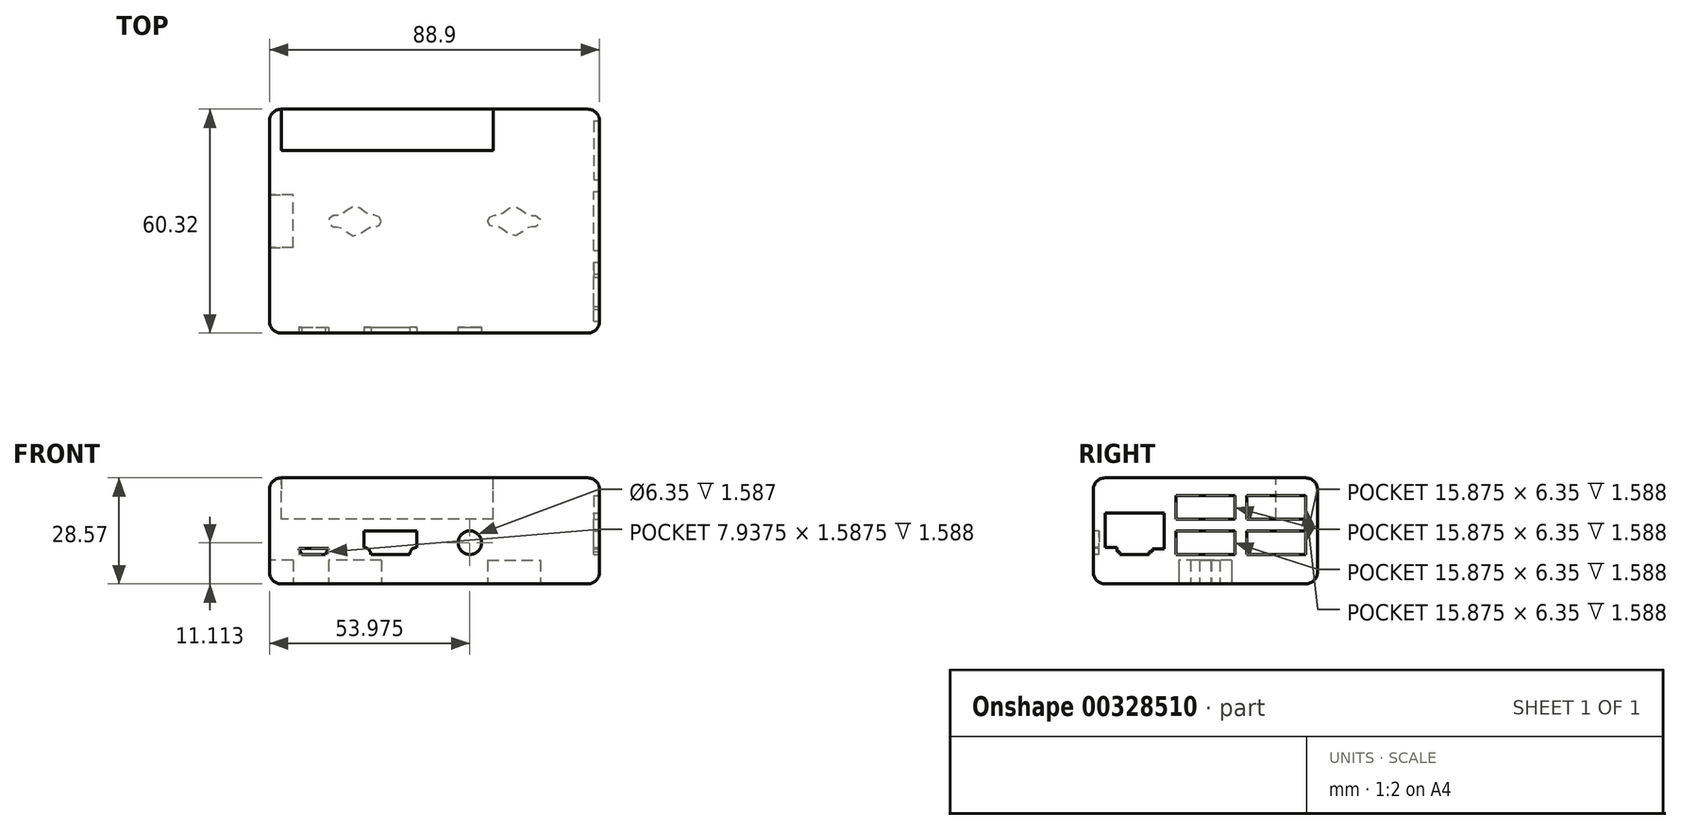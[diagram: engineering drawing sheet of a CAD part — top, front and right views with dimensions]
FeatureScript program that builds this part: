
annotation { "Feature Type Name" : "Feature", "Feature Type Description" : "" }
export const myFeature = defineFeature(function(context is Context, id is Id, definition is map)
    precondition{}
    {
        {
            var Q0;
            Q0=qCreatedBy(makeId("Top.planeOp"),FACE);
            var sketch = newSketch(context, id + "F0", { "sketchPlane" : qUnion([Q0])});
            skLineSegment(sketch, "E0.bottom", {"start": v(44.45, 30.16) * mm, "end": v(-44.45, 30.16) * mm});
            skLineSegment(sketch, "E0.top", {"start": v(44.45, -30.16) * mm, "end": v(-44.45, -30.16) * mm});
            skLineSegment(sketch, "E0.left", {"start": v(44.45, 30.16) * mm, "end": v(44.45, -30.16) * mm});
            skLineSegment(sketch, "E0.right", {"start": v(-44.45, 30.16) * mm, "end": v(-44.45, -30.16) * mm});
            skPoint(sketch, "E0.middle", {"position": v(0, 0) * mm});
            skLineSegment(sketch, "E1", {"start": v(0, 0) * mm, "end": v(14.29, 0) * mm});
            skLineSegment(sketch, "E2", {"start": v(0, 0) * mm, "end": v(-14.29, 0) * mm});
            skLineSegment(sketch, "E3", {"start": v(-14.29, 0) * mm, "end": v(-28.58, 0) * mm, "construction": true});
            skLineSegment(sketch, "E4", {"start": v(14.29, 0) * mm, "end": v(28.58, 0) * mm, "construction": true});
            skPoint(sketch, "E5", {"position": v(21.43, 0) * mm});
            skPoint(sketch, "E6", {"position": v(-21.43, 0) * mm});
            skLineSegment(sketch, "E7", {"start": v(14.29, 0) * mm, "end": v(15.88, 0) * mm, "construction": true});
            skLineSegment(sketch, "E8", {"start": v(28.58, 0) * mm, "end": v(26.99, 0) * mm, "construction": true});
            skLineSegment(sketch, "E9", {"start": v(-28.58, 0) * mm, "end": v(-26.99, 0) * mm, "construction": true});
            skLineSegment(sketch, "E10", {"start": v(-14.29, 0) * mm, "end": v(-15.88, 0) * mm, "construction": true});
            skLineSegment(sketch, "E11", {"start": v(-15.88, 0) * mm, "end": v(-15.88, 1.59) * mm, "construction": true});
            skLineSegment(sketch, "E12", {"start": v(-26.99, 0) * mm, "end": v(-26.99, 1.59) * mm, "construction": true});
            skLineSegment(sketch, "E13", {"start": v(-26.99, 0) * mm, "end": v(-26.99, -1.59) * mm, "construction": true});
            skLineSegment(sketch, "E14", {"start": v(-15.88, 0) * mm, "end": v(-15.88, -1.59) * mm, "construction": true});
            skLineSegment(sketch, "E15", {"start": v(15.88, 0) * mm, "end": v(15.88, -1.59) * mm, "construction": true});
            skLineSegment(sketch, "E16", {"start": v(26.99, 0) * mm, "end": v(26.99, 1.59) * mm, "construction": true});
            skLineSegment(sketch, "E17", {"start": v(15.88, 0) * mm, "end": v(15.88, 1.59) * mm, "construction": true});
            skLineSegment(sketch, "E18", {"start": v(26.99, 0) * mm, "end": v(26.99, -1.59) * mm, "construction": true});
            skLineSegment(sketch, "E19", {"start": v(21.43, 0) * mm, "end": v(21.43, 3.97) * mm, "construction": true});
            skLineSegment(sketch, "E20", {"start": v(21.43, 0) * mm, "end": v(21.43, -3.97) * mm, "construction": true});
            skLineSegment(sketch, "E21", {"start": v(15.88, 1.59) * mm, "end": v(17.46, 1.59) * mm, "construction": true});
            skLineSegment(sketch, "E22", {"start": v(15.88, -1.59) * mm, "end": v(17.46, -1.59) * mm, "construction": true});
            skLineSegment(sketch, "E23", {"start": v(26.99, 1.59) * mm, "end": v(25.4, 1.59) * mm, "construction": true});
            skLineSegment(sketch, "E24", {"start": v(26.99, -1.59) * mm, "end": v(25.4, -1.59) * mm, "construction": true});
            skFitSpline(sketch, "E25", {"points": [v(14.29, 0) * mm, v(15.88, 1.59) * mm, v(17.46, 1.59) * mm, v(21.43, 3.97) * mm, v(25.4, 1.59) * mm, v(26.99, 1.59) * mm, v(28.58, 0) * mm, v(26.99, -1.59) * mm, v(25.4, -1.59) * mm, v(21.43, -3.97) * mm, v(17.46, -1.59) * mm, v(15.88, -1.59) * mm, v(14.29, 0) * mm]});
            skLineSegment(sketch, "E26", {"start": v(0, 0) * mm, "end": v(0, 11.35) * mm, "construction": true});
            skLineSegment(sketch, "E27.MirrorCS", {"start": v(-15.88, 1.59) * mm, "end": v(-17.46, 1.59) * mm, "construction": true});
            skLineSegment(sketch, "E28.MirrorCS", {"start": v(-15.88, -1.59) * mm, "end": v(-17.46, -1.59) * mm, "construction": true});
            skLineSegment(sketch, "E29.MirrorCS", {"start": v(-26.99, -1.59) * mm, "end": v(-25.4, -1.59) * mm, "construction": true});
            skLineSegment(sketch, "E30.MirrorCS", {"start": v(-26.99, 1.59) * mm, "end": v(-25.4, 1.59) * mm, "construction": true});
            skLineSegment(sketch, "E31.MirrorCS", {"start": v(-21.43, 0) * mm, "end": v(-21.43, 3.97) * mm, "construction": true});
            skLineSegment(sketch, "E32.MirrorCS", {"start": v(-21.43, 0) * mm, "end": v(-21.43, -3.97) * mm, "construction": true});
            skFitSpline(sketch, "E33.MirrorC", {"points": [v(-14.29, 0) * mm, v(-15.88, 1.59) * mm, v(-17.46, 1.59) * mm, v(-21.43, 3.97) * mm, v(-25.4, 1.59) * mm, v(-26.99, 1.59) * mm, v(-28.58, 0) * mm, v(-26.99, -1.59) * mm, v(-25.4, -1.59) * mm, v(-21.43, -3.97) * mm, v(-17.46, -1.59) * mm, v(-15.88, -1.59) * mm, v(-14.29, 0) * mm]});
            skLineSegment(sketch, "E34", {"start": v(-44.45, 0) * mm, "end": v(-38.1, 0) * mm});
            skLineSegment(sketch, "E35", {"start": v(-38.1, 0) * mm, "end": v(-38.1, 7.14) * mm});
            skLineSegment(sketch, "E36", {"start": v(-38.1, 0) * mm, "end": v(-38.1, -7.14) * mm});
            skLineSegment(sketch, "E37", {"start": v(-38.1, -7.14) * mm, "end": v(-44.45, -7.14) * mm});
            skLineSegment(sketch, "E38", {"start": v(-38.1, 7.14) * mm, "end": v(-44.45, 7.14) * mm});
            skSolve(sketch);
        }
        {
            var Q0;
            Q0 = qSketchRegion(id + "F0", true);
            var Q1;
            Q1=makeQuery(id+"F0.imprint","IMPRINT",FACE,{"disambiguationData":[TD([[makeQuery(id+"F0.imprint","IMPRINT",EDGE,{"derivedFrom":sQuery(id+"F0.wireOp",EDGE,"E33.MirrorC")}),1.0]])]});
            var Q2;
            Q2=makeQuery(id+"F0.imprint","IMPRINT",FACE,{"disambiguationData":[TD([[makeQuery(id+"F0.imprint","IMPRINT",EDGE,{"derivedFrom":sQuery(id+"F0.wireOp",EDGE,"E25")}),-1.0]])]});
            extrude(context, id + "F1", {"entities" : qUnion([Q0, Q1, Q2]), "depth" : 28.57 * mm});
        }
        {
            var Q0;
            {var subQ0=sQuery(id+"F0.wireOp",EDGE,"E34");Q0=makeQuery(id+"F0.imprint","IMPRINT",FACE,{"disambiguationData":[TD([[makeQuery(id+"F0.imprint","IMPRINT",EDGE,{"derivedFrom":subQ0}),1.0]])]});}
            var Q1;
            {var subQ0=sQuery(id+"F0.wireOp",EDGE,"E34");Q1=makeQuery(id+"F0.imprint","IMPRINT",FACE,{"disambiguationData":[TD([[makeQuery(id+"F0.imprint","IMPRINT",EDGE,{"derivedFrom":subQ0}),-1.0]])]});}
            var Q2;
            Q2=makeQuery(id+"F0.imprint","IMPRINT",FACE,{"disambiguationData":[TD([[makeQuery(id+"F0.imprint","IMPRINT",EDGE,{"derivedFrom":sQuery(id+"F0.wireOp",EDGE,"E33.MirrorC")}),1.0]])]});
            var Q3;
            Q3=makeQuery(id+"F0.imprint","IMPRINT",FACE,{"disambiguationData":[TD([[makeQuery(id+"F0.imprint","IMPRINT",EDGE,{"derivedFrom":sQuery(id+"F0.wireOp",EDGE,"E25")}),-1.0]])]});
            extrude(context, id + "F2", {"entities" : qUnion([Q0, Q1, Q2, Q3]), "operationType" : NewBodyOperationType.REMOVE, "depth" : 6.35 * mm});
        }
        {
            var Q0;
            Q0=makeQuery(id+"F1.opExtrude","SWEPT_FACE",FACE,{"disambiguationData":[OSD([sQuery(id+"F0.wireOp",EDGE,"E0.top")])]});
            var sketch = newSketch(context, id + "F3", { "sketchPlane" : qUnion([Q0])});
            skLineSegment(sketch, "E39.0.0", {"start": v(-44.45, 0) * mm, "end": v(44.45, 0) * mm});
            skLineSegment(sketch, "E39.0.1", {"start": v(44.45, 0) * mm, "end": v(44.45, 28.58) * mm});
            skLineSegment(sketch, "E39.0.2", {"start": v(44.45, 28.58) * mm, "end": v(-44.45, 28.58) * mm});
            skLineSegment(sketch, "E39.0.3", {"start": v(-44.45, 28.58) * mm, "end": v(-44.45, 0) * mm});
            skLineSegment(sketch, "E40", {"start": v(-44.45, 0) * mm, "end": v(-44.45, 14.29) * mm, "construction": true});
            skLineSegment(sketch, "E41", {"start": v(-44.45, 14.29) * mm, "end": v(44.45, 14.29) * mm, "construction": true});
            skLineSegment(sketch, "E42", {"start": v(-44.45, 14.29) * mm, "end": v(-44.45, 7.94) * mm, "construction": true});
            skLineSegment(sketch, "E43", {"start": v(-44.45, 7.94) * mm, "end": v(44.45, 7.94) * mm, "construction": true});
            skLineSegment(sketch, "E44", {"start": v(-44.45, 14.29) * mm, "end": v(-19.05, 14.29) * mm, "construction": true});
            skLineSegment(sketch, "E45", {"start": v(-19.05, 14.29) * mm, "end": v(-4.76, 14.29) * mm, "construction": true});
            skLineSegment(sketch, "E46", {"start": v(-4.76, 14.29) * mm, "end": v(-4.76, 9.84) * mm, "construction": true});
            skLineSegment(sketch, "E47", {"start": v(-19.05, 14.29) * mm, "end": v(-19.05, 9.84) * mm});
            skLineSegment(sketch, "E48", {"start": v(-19.05, 14.29) * mm, "end": v(-4.76, 14.29) * mm});
            skLineSegment(sketch, "E49", {"start": v(-4.76, 14.29) * mm, "end": v(-4.76, 9.84) * mm});
            skLineSegment(sketch, "E50", {"start": v(-4.76, 14.29) * mm, "end": v(-6.35, 14.29) * mm, "construction": true});
            skLineSegment(sketch, "E51", {"start": v(-19.05, 14.29) * mm, "end": v(-17.46, 14.29) * mm, "construction": true});
            skLineSegment(sketch, "E52", {"start": v(-17.46, 14.29) * mm, "end": v(-17.46, 7.94) * mm, "construction": true});
            skLineSegment(sketch, "E53", {"start": v(-6.35, 14.29) * mm, "end": v(-6.35, 7.94) * mm, "construction": true});
            skLineSegment(sketch, "E54", {"start": v(-17.46, 7.94) * mm, "end": v(-6.35, 7.94) * mm});
            skPoint(sketch, "E55", {"position": v(-4.76, 7.94) * mm});
            skPoint(sketch, "E56", {"position": v(-19.05, 7.94) * mm});
            skArc(sketch, "E57", {"start": v(-19.05, 9.84) * mm, "mid": v(-17.7, 9.28) * mm, "end": v(-17.15, 7.94) * mm});
            skArc(sketch, "E58", {"start": v(-4.76, 9.84) * mm, "mid": v(-6.1, 9.28) * mm, "end": v(-6.67, 7.94) * mm});
            skLineSegment(sketch, "E59", {"start": v(-44.45, 7.94) * mm, "end": v(-36.51, 7.94) * mm, "construction": true});
            skLineSegment(sketch, "E60", {"start": v(-36.51, 7.94) * mm, "end": v(-28.58, 7.94) * mm, "construction": true});
            skLineSegment(sketch, "E61", {"start": v(-28.58, 7.94) * mm, "end": v(-28.58, 9.52) * mm, "construction": true});
            skLineSegment(sketch, "E62", {"start": v(-28.58, 9.52) * mm, "end": v(-36.51, 9.52) * mm, "construction": true});
            skLineSegment(sketch, "E63", {"start": v(-36.51, 9.52) * mm, "end": v(-36.51, 7.94) * mm, "construction": true});
            skLineSegment(sketch, "E64", {"start": v(-36.51, 9.52) * mm, "end": v(-28.58, 9.52) * mm});
            skLineSegment(sketch, "E65", {"start": v(-36.51, 7.94) * mm, "end": v(-35.72, 7.94) * mm});
            skLineSegment(sketch, "E66", {"start": v(-28.58, 7.94) * mm, "end": v(-29.37, 7.94) * mm});
            skLineSegment(sketch, "E67", {"start": v(-29.37, 7.94) * mm, "end": v(-28.58, 9.52) * mm});
            skLineSegment(sketch, "E68", {"start": v(-35.72, 7.94) * mm, "end": v(-36.51, 9.53) * mm});
            skLineSegment(sketch, "E69", {"start": v(-35.72, 7.94) * mm, "end": v(-29.37, 7.94) * mm});
            skLineSegment(sketch, "E70", {"start": v(-4.76, 14.29) * mm, "end": v(9.53, 14.29) * mm, "construction": true});
            skLineSegment(sketch, "E71", {"start": v(-4.76, 7.94) * mm, "end": v(9.53, 7.94) * mm, "construction": true});
            skLineSegment(sketch, "E72", {"start": v(9.53, 7.94) * mm, "end": v(9.53, 14.29) * mm, "construction": true});
            skPoint(sketch, "E73", {"position": v(9.53, 11.11) * mm});
            skCircle(sketch, "E74", {"center": v(9.53, 11.11) * mm, "radius": 3.18 * mm});
            skSolve(sketch);
        }
        {
            var Q0;
            Q0=makeQuery(id+"F1.opExtrude","SWEPT_FACE",FACE,{"disambiguationData":[OSD([sQuery(id+"F0.wireOp",EDGE,"E0.left")])]});
            var sketch = newSketch(context, id + "F4", { "sketchPlane" : qUnion([Q0])});
            skLineSegment(sketch, "E75", {"start": v(30.16, 0) * mm, "end": v(30.16, 7.94) * mm, "construction": true});
            skLineSegment(sketch, "E76", {"start": v(26.99, 7.94) * mm, "end": v(11.11, 7.94) * mm, "construction": true});
            skLineSegment(sketch, "E77", {"start": v(7.94, 7.94) * mm, "end": v(-7.94, 7.94) * mm, "construction": true});
            skLineSegment(sketch, "E78", {"start": v(-7.94, 7.94) * mm, "end": v(-11.11, 7.94) * mm, "construction": true});
            skLineSegment(sketch, "E79.bottom", {"start": v(26.99, 7.94) * mm, "end": v(11.11, 7.94) * mm});
            skLineSegment(sketch, "E79.top", {"start": v(26.99, 23.81) * mm, "end": v(11.11, 23.81) * mm});
            skLineSegment(sketch, "E79.left", {"start": v(26.99, 7.94) * mm, "end": v(26.99, 14.29) * mm});
            skLineSegment(sketch, "E79.right", {"start": v(11.11, 7.94) * mm, "end": v(11.11, 14.29) * mm});
            skLineSegment(sketch, "E80.bottom", {"start": v(-7.94, 7.94) * mm, "end": v(7.94, 7.94) * mm});
            skLineSegment(sketch, "E80.top", {"start": v(-7.94, 23.81) * mm, "end": v(7.94, 23.81) * mm});
            skLineSegment(sketch, "E80.left", {"start": v(-7.94, 7.94) * mm, "end": v(-7.94, 14.29) * mm});
            skLineSegment(sketch, "E80.right", {"start": v(7.94, 7.94) * mm, "end": v(7.94, 14.29) * mm});
            skLineSegment(sketch, "E81.top", {"start": v(-26.99, 19.05) * mm, "end": v(-11.11, 19.05) * mm});
            skLineSegment(sketch, "E81.left", {"start": v(-26.99, 9.8) * mm, "end": v(-26.99, 19.05) * mm});
            skLineSegment(sketch, "E81.right", {"start": v(-11.11, 9.5) * mm, "end": v(-11.11, 19.05) * mm});
            skLineSegment(sketch, "E82.top", {"start": v(-7.94, 17.46) * mm, "end": v(7.94, 17.46) * mm});
            skLineSegment(sketch, "E82.left", {"start": v(-7.94, 23.81) * mm, "end": v(-7.94, 17.46) * mm});
            skLineSegment(sketch, "E82.right", {"start": v(7.94, 23.81) * mm, "end": v(7.94, 17.46) * mm});
            skLineSegment(sketch, "E83.bottom", {"start": v(11.11, 23.81) * mm, "end": v(26.99, 23.81) * mm});
            skLineSegment(sketch, "E83.top", {"start": v(11.11, 17.46) * mm, "end": v(26.99, 17.46) * mm});
            skLineSegment(sketch, "E83.left", {"start": v(11.11, 23.81) * mm, "end": v(11.11, 17.46) * mm});
            skLineSegment(sketch, "E83.right", {"start": v(26.99, 23.81) * mm, "end": v(26.99, 17.46) * mm});
            skLineSegment(sketch, "E84.top", {"start": v(-7.94, 14.29) * mm, "end": v(7.94, 14.29) * mm});
            skLineSegment(sketch, "E85.bottom", {"start": v(11.11, 7.94) * mm, "end": v(26.99, 7.94) * mm});
            skLineSegment(sketch, "E85.top", {"start": v(11.11, 14.29) * mm, "end": v(26.99, 14.29) * mm});
            skLineSegment(sketch, "E86.top", {"start": v(-26.99, 9.8) * mm, "end": v(-23.81, 9.8) * mm});
            skLineSegment(sketch, "E86.right", {"start": v(-23.81, 8.73) * mm, "end": v(-23.81, 9.8) * mm});
            skLineSegment(sketch, "E87.top", {"start": v(-11.11, 9.5) * mm, "end": v(-14.29, 9.5) * mm});
            skLineSegment(sketch, "E87.right", {"start": v(-14.29, 8.73) * mm, "end": v(-14.29, 9.5) * mm});
            skLineSegment(sketch, "E88.top", {"start": v(-23.81, 8.73) * mm, "end": v(-23.02, 8.73) * mm});
            skLineSegment(sketch, "E88.right", {"start": v(-23.02, 7.94) * mm, "end": v(-23.02, 8.73) * mm});
            skLineSegment(sketch, "E89.top", {"start": v(-14.29, 8.73) * mm, "end": v(-15.08, 8.73) * mm});
            skLineSegment(sketch, "E89.right", {"start": v(-15.08, 7.94) * mm, "end": v(-15.08, 8.73) * mm});
            skLineSegment(sketch, "E90.trimOffspring", {"start": v(-26.99, 7.94) * mm, "end": v(-30.16, 7.94) * mm, "construction": true});
            skLineSegment(sketch, "E91.trimOffspring", {"start": v(-23.02, 7.94) * mm, "end": v(-15.08, 7.94) * mm});
            skLineSegment(sketch, "E92.trimOffspring", {"start": v(-15.08, 7.94) * mm, "end": v(-23.02, 7.94) * mm, "construction": true});
            skLineSegment(sketch, "E93.trimOffspring", {"start": v(-7.94, 17.46) * mm, "end": v(-7.94, 23.81) * mm});
            skLineSegment(sketch, "E94.trimOffspring", {"start": v(7.94, 17.46) * mm, "end": v(7.94, 23.81) * mm});
            skLineSegment(sketch, "E95.trimOffspring", {"start": v(11.11, 17.46) * mm, "end": v(11.11, 23.81) * mm});
            skLineSegment(sketch, "E96.trimOffspring", {"start": v(26.99, 17.46) * mm, "end": v(26.99, 23.81) * mm});
            skLineSegment(sketch, "E97.trimOffspring", {"start": v(7.94, 7.94) * mm, "end": v(-11.11, 7.94) * mm, "construction": true});
            skSolve(sketch);
        }
        {
            var Q0;
            Q0 = qSketchRegion(id + "F4", true);
            extrude(context, id + "F5", {"entities" : qUnion([Q0]), "operationType" : NewBodyOperationType.REMOVE, "oppositeDirection" : true, "depth" : 1.59 * mm});
        }
        {
            var Q0;
            Q0=makeQuery(id+"F3.imprint","IMPRINT",FACE,{"disambiguationData":[TD([[makeQuery(id+"F3.imprint","IMPRINT",EDGE,{"derivedFrom":sQuery(id+"F3.wireOp",EDGE,"E64")}),-1.0]])]});
            var Q1;
            Q1=makeQuery(id+"F3.imprint","IMPRINT",FACE,{"disambiguationData":[TD([[makeQuery(id+"F3.imprint","IMPRINT",EDGE,{"derivedFrom":sQuery(id+"F3.wireOp",EDGE,"E47")}),1.0]])]});
            var Q2;
            Q2=makeQuery(id+"F3.imprint","IMPRINT",FACE,{"disambiguationData":[TD([[makeQuery(id+"F3.imprint","IMPRINT",EDGE,{"derivedFrom":sQuery(id+"F3.wireOp",EDGE,"E74")}),1.0]])]});
            extrude(context, id + "F6", {"entities" : qUnion([Q0, Q1, Q2]), "operationType" : NewBodyOperationType.REMOVE, "oppositeDirection" : true, "depth" : 1.59 * mm});
        }
        {
            var Q0;
            Q0=makeQuery(id+"F1.opExtrude","CAP_FACE",FACE,{"disambiguationData":[OSD([sQuery(id+"F0.wireOp",EDGE,"E0.bottom"),sQuery(id+"F0.wireOp",EDGE,"E0.top"),sQuery(id+"F0.wireOp",EDGE,"E0.left"),sQuery(id+"F0.wireOp",EDGE,"E0.right")])],"isStart":false});
            var sketch = newSketch(context, id + "F7", { "sketchPlane" : qUnion([Q0])});
            skLineSegment(sketch, "E98.0.0", {"start": v(-44.45, 30.16) * mm, "end": v(-44.45, -30.16) * mm});
            skLineSegment(sketch, "E98.0.1", {"start": v(-44.45, -30.16) * mm, "end": v(44.45, -30.16) * mm});
            skLineSegment(sketch, "E98.0.2", {"start": v(44.45, -30.16) * mm, "end": v(44.45, 30.16) * mm});
            skLineSegment(sketch, "E98.0.3", {"start": v(44.45, 30.16) * mm, "end": v(-44.45, 30.16) * mm});
            skLineSegment(sketch, "E99", {"start": v(-44.45, 30.16) * mm, "end": v(-41.28, 30.16) * mm, "construction": true});
            skLineSegment(sketch, "E100", {"start": v(-41.28, 30.16) * mm, "end": v(-41.28, 19.05) * mm});
            skLineSegment(sketch, "E101", {"start": v(-41.28, 19.05) * mm, "end": v(15.88, 19.05) * mm});
            skLineSegment(sketch, "E102", {"start": v(15.88, 19.05) * mm, "end": v(15.88, 30.16) * mm});
            skSolve(sketch);
        }
        {
            var Q0;
            {var subQ0=sQuery(id+"F7.wireOp",EDGE,"E100");Q0=makeQuery(id+"F7.imprint","IMPRINT",FACE,{"disambiguationData":[TD([[makeQuery(id+"F7.imprint","IMPRINT",EDGE,{"derivedFrom":subQ0}),1.0]])]});}
            extrude(context, id + "F8", {"entities" : qUnion([Q0]), "operationType" : NewBodyOperationType.REMOVE, "oppositeDirection" : true, "depth" : 11.1 * mm});
        }
        {
            var Q0;
            Q0=makeQuery(id+"F1.opExtrude","CAP_EDGE",EDGE,{"disambiguationData":[OSD([sQuery(id+"F0.wireOp",EDGE,"E0.top")])],"isStart":false});
            var Q1;
            Q1=makeQuery(id+"F1.opExtrude","CAP_EDGE",EDGE,{"disambiguationData":[OSD([sQuery(id+"F0.wireOp",EDGE,"E0.right")])],"isStart":false});
            var Q2;
            Q2=makeQuery(id+"F1.opExtrude","CAP_EDGE",EDGE,{"disambiguationData":[OSD([sQuery(id+"F0.wireOp",EDGE,"E0.left")])],"isStart":false});
            var Q3;
            Q3=makeQuery(id+"F1.opExtrude","SWEPT_EDGE",EDGE,{"disambiguationData":[OSD([sQuery(id+"F0.wireOp",EDGE,"E0.top"),sQuery(id+"F0.wireOp",EDGE,"E0.left")])]});
            var Q4;
            Q4=makeQuery(id+"F1.opExtrude","CAP_EDGE",EDGE,{"disambiguationData":[OSD([sQuery(id+"F0.wireOp",EDGE,"E0.top")])],"isStart":true});
            var Q5;
            Q5=makeQuery(id+"F1.opExtrude","CAP_EDGE",EDGE,{"disambiguationData":[OSD([sQuery(id+"F0.wireOp",EDGE,"E0.left")])],"isStart":true});
            var Q6;
            Q6=makeQuery(id+"F1.opExtrude","SWEPT_EDGE",EDGE,{"disambiguationData":[OSD([sQuery(id+"F0.wireOp",EDGE,"E0.bottom"),sQuery(id+"F0.wireOp",EDGE,"E0.left")])]});
            var Q7;
            Q7=makeQuery(id+"F1.opExtrude","CAP_EDGE",EDGE,{"disambiguationData":[OSD([sQuery(id+"F0.wireOp",EDGE,"E0.bottom")])],"isStart":false});
            var Q8;
            Q8=makeQuery(id+"F1.opExtrude","CAP_EDGE",EDGE,{"disambiguationData":[OSD([sQuery(id+"F0.wireOp",EDGE,"E0.bottom")])],"isStart":true});
            var Q9;
            Q9=makeQuery(id+"F1.opExtrude","SWEPT_EDGE",EDGE,{"disambiguationData":[OSD([sQuery(id+"F0.wireOp",EDGE,"E0.bottom"),sQuery(id+"F0.wireOp",EDGE,"E0.right")])]});
            var Q10;
            {var subQ0=sQuery(id+"F0.wireOp",EDGE,"E0.bottom");var subQ1=sQuery(id+"F0.wireOp",EDGE,"E0.right");Q10=makeQuery(id+"F2.boolean.opBoolean","SPLIT",EDGE,{"disambiguationData":[TD([makeQuery(id+"F1.opExtrude","SWEPT_FACE",FACE,{"disambiguationData":[OSD([subQ0])]})])],"derivedFrom":makeQuery(id+"F1.opExtrude","CAP_EDGE",EDGE,{"disambiguationData":[OSD([subQ1])],"isStart":true})});}
            var Q11;
            {var subQ0=sQuery(id+"F0.wireOp",EDGE,"E0.right");var subQ1=sQuery(id+"F0.wireOp",EDGE,"E0.top");Q11=makeQuery(id+"F2.boolean.opBoolean","SPLIT",EDGE,{"disambiguationData":[TD([makeQuery(id+"F1.opExtrude","SWEPT_FACE",FACE,{"disambiguationData":[OSD([subQ1])]})])],"derivedFrom":makeQuery(id+"F1.opExtrude","CAP_EDGE",EDGE,{"disambiguationData":[OSD([subQ0])],"isStart":true})});}
            var Q12;
            Q12=makeQuery(id+"F1.opExtrude","SWEPT_EDGE",EDGE,{"disambiguationData":[OSD([sQuery(id+"F0.wireOp",EDGE,"E0.top"),sQuery(id+"F0.wireOp",EDGE,"E0.right")])]});
            fillet(context, id + "F9", {"entities" : qUnion([Q0, Q1, Q2, Q3, Q4, Q5, Q6, Q7, Q8, Q9, Q10, Q11, Q12]), "radius" : 3.17 * mm, "tangentPropagation" : true, "allowEdgeOverflow" : false});
        }
    });
